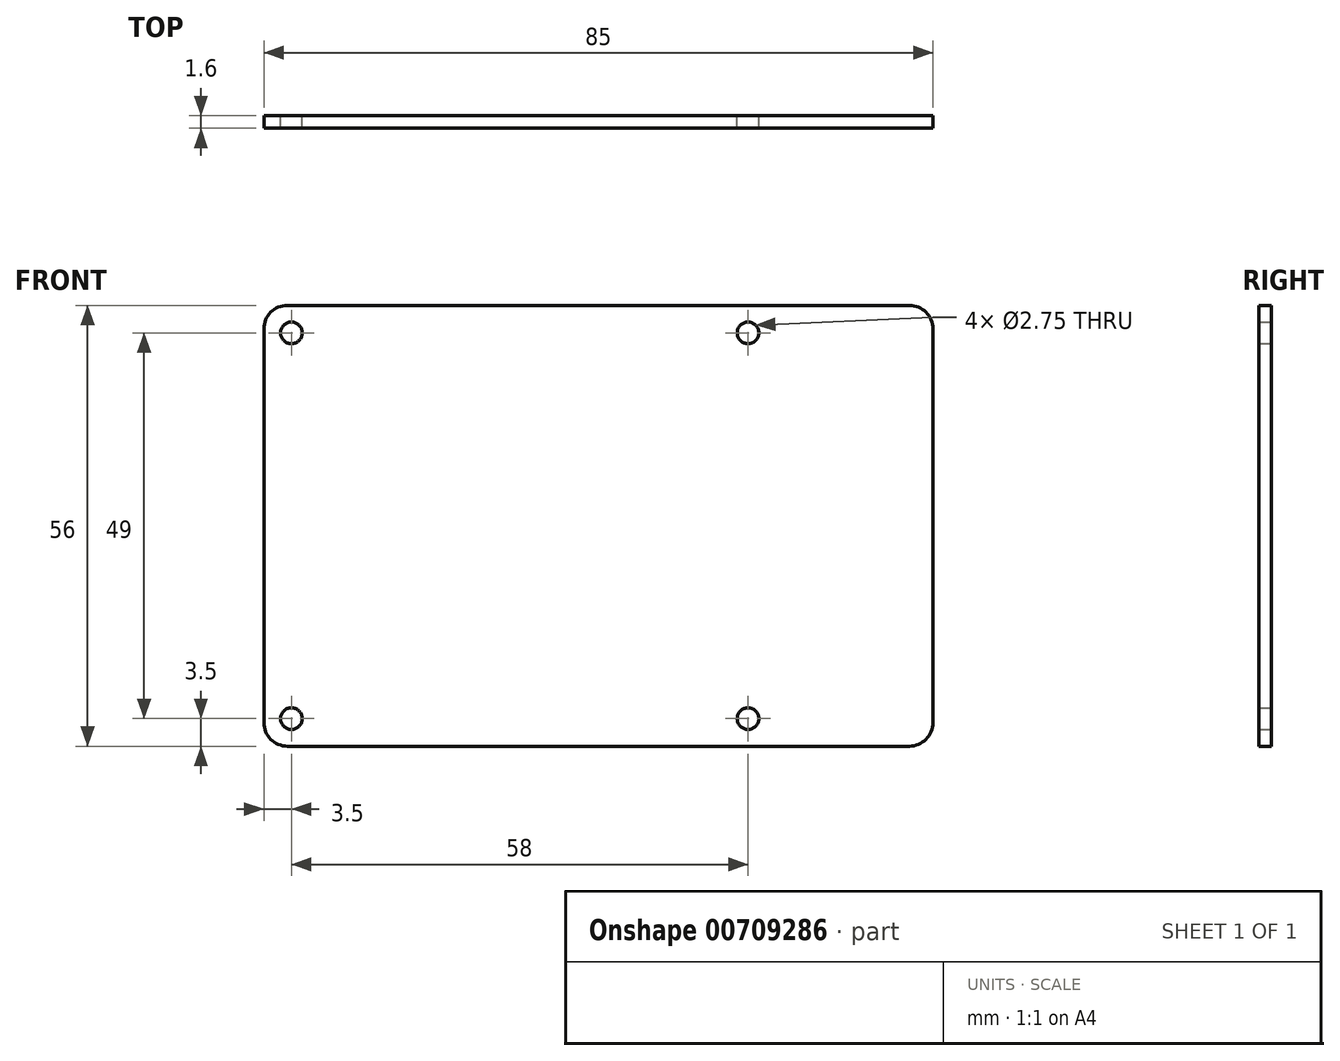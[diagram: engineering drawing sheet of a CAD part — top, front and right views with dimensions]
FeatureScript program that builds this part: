
annotation { "Feature Type Name" : "Feature", "Feature Type Description" : "" }
export const myFeature = defineFeature(function(context is Context, id is Id, definition is map)
    precondition{}
    {
        {
            var Q0;
            Q0=qCreatedBy(makeId("Front.planeOp"),FACE);
            var sketch = newSketch(context, id + "F0", { "sketchPlane" : qUnion([Q0])});
            skLineSegment(sketch, "E0.bottom", {"start": v(-42.5, -28) * mm, "end": v(42.5, -28) * mm});
            skLineSegment(sketch, "E0.top", {"start": v(-42.5, 28) * mm, "end": v(42.5, 28) * mm});
            skLineSegment(sketch, "E0.left", {"start": v(-42.5, -28) * mm, "end": v(-42.5, 28) * mm});
            skLineSegment(sketch, "E0.right", {"start": v(42.5, -28) * mm, "end": v(42.5, 28) * mm});
            skPoint(sketch, "E0.middle", {"position": v(0, 0) * mm});
            skCircle(sketch, "E1", {"center": v(-39, 24.5) * mm, "radius": 1.38 * mm});
            skCircle(sketch, "E2", {"center": v(-39, -24.5) * mm, "radius": 1.38 * mm});
            skCircle(sketch, "E3", {"center": v(19, -24.5) * mm, "radius": 1.38 * mm});
            skCircle(sketch, "E4", {"center": v(19, 24.5) * mm, "radius": 1.38 * mm});
            skSolve(sketch);
        }
        {
            var Q0;
            Q0=makeQuery(id+"F0.imprint","IMPRINT",FACE,{"disambiguationData":[TD([[makeQuery(id+"F0.imprint","IMPRINT",EDGE,{"derivedFrom":sQuery(id+"F0.wireOp",EDGE,"E0.bottom")}),1.0]])]});
            extrude(context, id + "F1", {"entities" : qUnion([Q0]), "endBound" : BoundingType.SYMMETRIC, "depth" : 1.6 * mm, "offsetDistance" : 25 * mm});
        }
        {
            var Q0;
            Q0=makeQuery(id+"F1.opExtrude","SWEPT_EDGE",EDGE,{"disambiguationData":[OSD([sQuery(id+"F0.wireOp",EDGE,"E0.top"),sQuery(id+"F0.wireOp",EDGE,"E0.left")])]});
            var Q1;
            Q1=makeQuery(id+"F1.opExtrude","SWEPT_EDGE",EDGE,{"disambiguationData":[OSD([sQuery(id+"F0.wireOp",EDGE,"E0.top"),sQuery(id+"F0.wireOp",EDGE,"E0.right")])]});
            var Q2;
            Q2=makeQuery(id+"F1.opExtrude","SWEPT_EDGE",EDGE,{"disambiguationData":[OSD([sQuery(id+"F0.wireOp",EDGE,"E0.bottom"),sQuery(id+"F0.wireOp",EDGE,"E0.left")])]});
            var Q3;
            Q3=makeQuery(id+"F1.opExtrude","SWEPT_EDGE",EDGE,{"disambiguationData":[OSD([sQuery(id+"F0.wireOp",EDGE,"E0.bottom"),sQuery(id+"F0.wireOp",EDGE,"E0.right")])]});
            fillet(context, id + "F2", {"entities" : qUnion([Q0, Q1, Q2, Q3]), "radius" : 3 * mm, "tangentPropagation" : true, "allowEdgeOverflow" : false});
        }
    });
